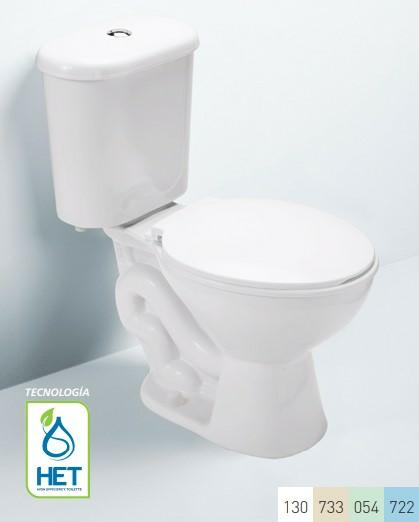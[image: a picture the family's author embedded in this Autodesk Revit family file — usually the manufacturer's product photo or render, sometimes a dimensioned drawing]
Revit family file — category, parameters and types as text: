
# Revit family: BRG-GRF-CCN_BELA MEZCLADORA DUCHA v_02
name_source: partatom
category: Aparatos sanitarios
units: mm (PartAtom-declared; Revit-internal decimal feet)

## family parameters
Anfitrión = Muro
Compartido = No
Corte con vacíos al cargar = No
Cota de conector redondo = Diámetro de uso
Número OmniClass = 23.45.00.00
Punto de cálculo de habitación = No
Siempre vertical = Sí
Tipo de pieza = Normal
Título OmniClass = Sanitary, Laundry, and Cleaning Equipment

## types (1)
- BELA MEZCLADORA MONOMANDO DE DUCHA
    Fabricante = BRIGGS ECUADOR
    Modelo = BELA MEZCLADORA MONOMANDO DE DUCHA
    URL = https://www.briggs.com.ec
    _EDESA_ Alto en cm = 13.6
    _EDESA_ Ancho en cm = 11.3
    _EDESA_ Categoría = Productos > Grifería > Ducha
    _EDESA_ Certificación = Cumple con norma NTE - INEN 3123 basada en la norma ASME 112.18.1 - 2012.
    _EDESA_ Color = Cromo
    _EDESA_ Conexión hidráulica = Entrada de agua: tubería ø 1/2"
    _EDESA_ Consumo/capacidad de agua en L = 9.5 litros por minuto / 2.5 gpm en combinación con cualquiera de nuestras regaderas
    _EDESA_ Descripción = Grifería monomando de ducha para agua fría y caliente. Instalación empotrado en la pared.
    _EDESA_ Garantía = De por vida para el cuerpo principal y acabado en cromo (306)
    _EDESA_ Manual de instalación = https://www.briggs.com.ec
    _EDESA_ Marca = BRIGGS
    _EDESA_ Materiales = Latón
    _EDESA_ Nombre = BELA MEZCLADORA MONOMANDO DE DUCHA
    _EDESA_ Productos necesarios para instalación = Regadera
    _EDESA_ Profundidad en cm = 8.5
    _EDESA_ Sku/código = SG0087173061CW
    _EDESA_ Tipo de instalación = Empotrado en la pared
